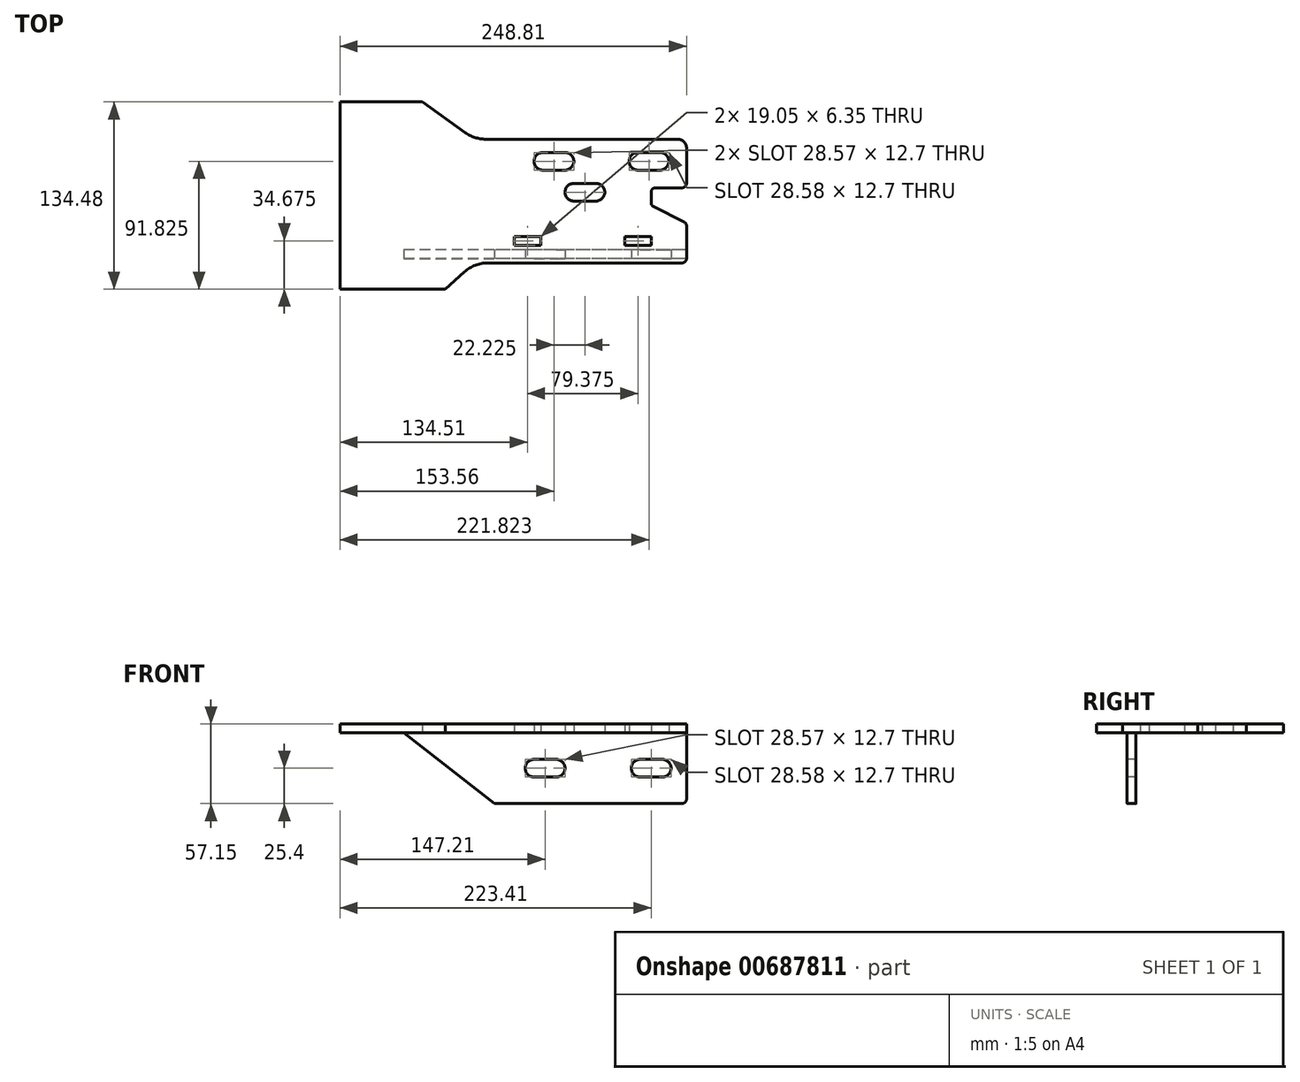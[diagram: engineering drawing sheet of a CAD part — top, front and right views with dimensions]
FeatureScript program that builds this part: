
annotation { "Feature Type Name" : "Feature", "Feature Type Description" : "" }
export const myFeature = defineFeature(function(context is Context, id is Id, definition is map)
    precondition{}
    {
        {
            var Q0;
            Q0=qCreatedBy(makeId("Top.planeOp"),FACE);
            var sketch = newSketch(context, id + "F0", { "sketchPlane" : qUnion([Q0])});
            skLineSegment(sketch, "E0.bottom", {"start": v(-68.04, 44.45) * mm, "end": v(76.2, 44.45) * mm});
            skLineSegment(sketch, "E0.top", {"start": v(-66.48, -44.45) * mm, "end": v(76.2, -44.45) * mm});
            skLineSegment(sketch, "E0.right", {"start": v(76.2, 44.45) * mm, "end": v(76.2, -44.45) * mm});
            skPoint(sketch, "E0.middle", {"position": v(0, 0) * mm});
            skCircle(sketch, "E1", {"center": v(-19.05, 28.58) * mm, "radius": 6.35 * mm});
            skCircle(sketch, "E2", {"center": v(57.15, 28.58) * mm, "radius": 6.35 * mm});
            skCircle(sketch, "E3", {"center": v(3.18, 6.35) * mm, "radius": 6.35 * mm});
            skLineSegment(sketch, "E4.bottom", {"start": v(-28.57, -31.75) * mm, "end": v(-47.62, -31.75) * mm});
            skLineSegment(sketch, "E4.top", {"start": v(-28.57, -25.4) * mm, "end": v(-47.62, -25.4) * mm});
            skLineSegment(sketch, "E4.left", {"start": v(-28.57, -31.75) * mm, "end": v(-28.57, -25.4) * mm});
            skLineSegment(sketch, "E4.right", {"start": v(-47.62, -31.75) * mm, "end": v(-47.62, -25.4) * mm});
            skPoint(sketch, "E4.middle", {"position": v(-38.1, -28.57) * mm});
            skLineSegment(sketch, "E5.bottom", {"start": v(50.8, -31.75) * mm, "end": v(31.75, -31.75) * mm});
            skLineSegment(sketch, "E5.top", {"start": v(50.8, -25.4) * mm, "end": v(31.75, -25.4) * mm});
            skLineSegment(sketch, "E5.left", {"start": v(50.8, -31.75) * mm, "end": v(50.8, -25.4) * mm});
            skLineSegment(sketch, "E5.right", {"start": v(31.75, -31.75) * mm, "end": v(31.75, -25.4) * mm});
            skPoint(sketch, "E5.middle", {"position": v(41.27, -28.57) * mm});
            skLineSegment(sketch, "E6", {"start": v(76.2, 9.53) * mm, "end": v(50.8, 9.53) * mm});
            skLineSegment(sketch, "E7", {"start": v(50.8, 9.52) * mm, "end": v(50.8, -3.18) * mm});
            skLineSegment(sketch, "E8", {"start": v(50.8, -3.18) * mm, "end": v(76.2, -15.88) * mm});
            skLineSegment(sketch, "E9", {"start": v(-82.83, 49.2) * mm, "end": v(-113.59, 71.23) * mm});
            skLineSegment(sketch, "E10", {"start": v(-97.17, -63.25) * mm, "end": v(-83.44, -50.94) * mm});
            skPoint(sketch, "E11.visualSharp", {"position": v(-76.2, 44.45) * mm});
            skArc(sketch, "E11.filletArc", {"start": v(-82.83, 49.2) * mm, "mid": v(-75.8, 45.67) * mm, "end": v(-68.04, 44.45) * mm});
            skPoint(sketch, "E12.visualSharp", {"position": v(-76.2, -44.45) * mm});
            skArc(sketch, "E12.filletArc", {"start": v(-66.48, -44.45) * mm, "mid": v(-75.56, -46.13) * mm, "end": v(-83.44, -50.94) * mm});
            skLineSegment(sketch, "E13", {"start": v(-97.17, -63.25) * mm, "end": v(-172.6, -63.25) * mm});
            skLineSegment(sketch, "E14", {"start": v(-172.6, -63.25) * mm, "end": v(-172.6, 71.23) * mm});
            skLineSegment(sketch, "E15", {"start": v(-172.6, 71.23) * mm, "end": v(-113.59, 71.23) * mm});
            skLineSegment(sketch, "E16", {"start": v(-26.99, 28.57) * mm, "end": v(-11.11, 28.58) * mm});
            skLineSegment(sketch, "E17", {"start": v(41.27, 28.58) * mm, "end": v(57.15, 28.58) * mm});
            skLineSegment(sketch, "E18", {"start": v(-4.76, 6.35) * mm, "end": v(11.11, 6.35) * mm});
            skArc(sketch, "E19.0.startCap", {"start": v(-26.99, 22.23) * mm, "mid": v(-33.34, 28.57) * mm, "end": v(-26.99, 34.93) * mm});
            skArc(sketch, "E19.0.endCap", {"start": v(-11.11, 34.93) * mm, "mid": v(-4.76, 28.57) * mm, "end": v(-11.11, 22.23) * mm});
            skLineSegment(sketch, "E19.0.left", {"start": v(-26.99, 34.92) * mm, "end": v(-11.11, 34.93) * mm});
            skLineSegment(sketch, "E19.0.right", {"start": v(-26.99, 22.23) * mm, "end": v(-11.11, 22.23) * mm});
            skArc(sketch, "E19.1.startCap", {"start": v(-4.76, 0) * mm, "mid": v(-11.11, 6.35) * mm, "end": v(-4.76, 12.7) * mm});
            skArc(sketch, "E19.1.endCap", {"start": v(11.11, 12.7) * mm, "mid": v(17.46, 6.35) * mm, "end": v(11.11, 0) * mm});
            skLineSegment(sketch, "E19.1.left", {"start": v(-4.76, 12.7) * mm, "end": v(11.11, 12.7) * mm});
            skLineSegment(sketch, "E19.1.right", {"start": v(-4.76, 0) * mm, "end": v(11.11, 0) * mm});
            skArc(sketch, "E19.2.startCap", {"start": v(41.27, 22.22) * mm, "mid": v(34.92, 28.57) * mm, "end": v(41.27, 34.92) * mm});
            skArc(sketch, "E19.2.endCap", {"start": v(57.15, 34.93) * mm, "mid": v(63.5, 28.58) * mm, "end": v(57.15, 22.23) * mm});
            skLineSegment(sketch, "E19.2.left", {"start": v(41.27, 34.93) * mm, "end": v(57.15, 34.93) * mm});
            skLineSegment(sketch, "E19.2.right", {"start": v(41.27, 22.23) * mm, "end": v(57.15, 22.23) * mm});
            skSolve(sketch);
        }
        {
            var Q0;
            {var subQ3=sQuery(id+"F0.wireOp",EDGE,"E0.bottom");Q0=makeQuery(id+"F0.imprint","IMPRINT",FACE,{"disambiguationData":[TD([[makeQuery(id+"F0.imprint","IMPRINT",EDGE,{"derivedFrom":subQ3}),-1.0]])]});}
            extrude(context, id + "F1", {"entities" : qUnion([Q0]), "depth" : 6.35 * mm, "offsetDistance" : 25.4 * mm});
        }
        {
            var Q0;
            Q0=makeQuery(id+"F1.opExtrude","CAP_FACE",FACE,{"disambiguationData":[OSD([sQuery(id+"F0.wireOp",EDGE,"E0.bottom"),sQuery(id+"F0.wireOp",EDGE,"E0.top"),sQuery(id+"F0.wireOp",EDGE,"E0.right"),sQuery(id+"F0.wireOp",EDGE,"E2"),sQuery(id+"F0.wireOp",EDGE,"E4.bottom"),sQuery(id+"F0.wireOp",EDGE,"E4.top"),sQuery(id+"F0.wireOp",EDGE,"E4.left"),sQuery(id+"F0.wireOp",EDGE,"E4.right"),sQuery(id+"F0.wireOp",EDGE,"E5.bottom"),sQuery(id+"F0.wireOp",EDGE,"E5.top"),sQuery(id+"F0.wireOp",EDGE,"E5.left"),sQuery(id+"F0.wireOp",EDGE,"E5.right"),sQuery(id+"F0.wireOp",EDGE,"E6"),sQuery(id+"F0.wireOp",EDGE,"E7"),sQuery(id+"F0.wireOp",EDGE,"E8"),sQuery(id+"F0.wireOp",EDGE,"E9"),sQuery(id+"F0.wireOp",EDGE,"E10"),sQuery(id+"F0.wireOp",EDGE,"E11.filletArc"),sQuery(id+"F0.wireOp",EDGE,"E12.filletArc"),sQuery(id+"F0.wireOp",EDGE,"E13"),sQuery(id+"F0.wireOp",EDGE,"E14"),sQuery(id+"F0.wireOp",EDGE,"E15"),sQuery(id+"F0.wireOp",EDGE,"E19.0.startCap"),sQuery(id+"F0.wireOp",EDGE,"E19.0.endCap"),sQuery(id+"F0.wireOp",EDGE,"E19.0.left"),sQuery(id+"F0.wireOp",EDGE,"E19.0.right"),sQuery(id+"F0.wireOp",EDGE,"E19.1.startCap"),sQuery(id+"F0.wireOp",EDGE,"E19.1.endCap"),sQuery(id+"F0.wireOp",EDGE,"E19.1.left"),sQuery(id+"F0.wireOp",EDGE,"E19.1.right"),sQuery(id+"F0.wireOp",EDGE,"E19.2.startCap"),sQuery(id+"F0.wireOp",EDGE,"E19.2.left"),sQuery(id+"F0.wireOp",EDGE,"E19.2.right")])],"isStart":true});
            var sketch = newSketch(context, id + "F2", { "sketchPlane" : qUnion([Q0])});
            skLineSegment(sketch, "E20.bottom", {"start": v(76.2, 41.27) * mm, "end": v(-152, 41.27) * mm});
            skLineSegment(sketch, "E20.top", {"start": v(76.2, 34.92) * mm, "end": v(-152, 34.92) * mm});
            skLineSegment(sketch, "E20.left", {"start": v(76.2, 41.27) * mm, "end": v(76.2, 34.92) * mm});
            skLineSegment(sketch, "E20.right", {"start": v(-152, 41.27) * mm, "end": v(-152, 34.92) * mm});
            skSolve(sketch);
        }
        {
            var Q0;
            Q0 = qSketchRegion(id + "F2", true);
            extrude(context, id + "F3", {"entities" : qUnion([Q0]), "depth" : 50.8 * mm, "offsetDistance" : 25.4 * mm});
        }
        {
            var Q0;
            Q0=makeQuery(id+"F3.opExtrude","SWEPT_FACE",FACE,{"disambiguationData":[OSD([sQuery(id+"F2.wireOp",EDGE,"E20.bottom")])]});
            var sketch = newSketch(context, id + "F4", { "sketchPlane" : qUnion([Q0])});
            skLineSegment(sketch, "E21", {"start": v(58.74, -25.4) * mm, "end": v(50.8, -25.4) * mm});
            skPoint(sketch, "E21.startSnap0", {"position": v(76.2, -25.4) * mm});
            skLineSegment(sketch, "E22", {"start": v(-33.34, -25.4) * mm, "end": v(-25.4, -25.4) * mm});
            skArc(sketch, "E23.0.startCap", {"start": v(-33.34, -31.75) * mm, "mid": v(-39.69, -25.4) * mm, "end": v(-33.34, -19.05) * mm});
            skArc(sketch, "E23.0.endCap", {"start": v(-17.46, -19.05) * mm, "mid": v(-11.11, -25.4) * mm, "end": v(-17.46, -31.75) * mm});
            skLineSegment(sketch, "E23.0.left", {"start": v(-33.34, -19.05) * mm, "end": v(-17.46, -19.05) * mm});
            skLineSegment(sketch, "E23.0.right", {"start": v(-33.34, -31.75) * mm, "end": v(-17.46, -31.75) * mm});
            skArc(sketch, "E23.1.startCap", {"start": v(58.74, -19.05) * mm, "mid": v(65.09, -25.4) * mm, "end": v(58.74, -31.75) * mm});
            skArc(sketch, "E23.1.endCap", {"start": v(42.86, -31.75) * mm, "mid": v(36.51, -25.4) * mm, "end": v(42.86, -19.05) * mm});
            skLineSegment(sketch, "E23.1.left", {"start": v(58.74, -31.75) * mm, "end": v(42.86, -31.75) * mm});
            skLineSegment(sketch, "E23.1.right", {"start": v(58.74, -19.05) * mm, "end": v(42.86, -19.05) * mm});
            skLineSegment(sketch, "E24", {"start": v(-25.4, -25.4) * mm, "end": v(-17.46, -25.4) * mm});
            skLineSegment(sketch, "E25", {"start": v(50.8, -25.4) * mm, "end": v(42.86, -25.4) * mm});
            skLineSegment(sketch, "E26", {"start": v(-126.98, 0) * mm, "end": v(-61.91, -50.8) * mm});
            skSolve(sketch);
        }
        {
            var Q0;
            Q0 = qSketchRegion(id + "F4", true);
            var Q1;
            {var subQ0=sQuery(id+"F4.wireOp",EDGE,"E26");Q1=makeQuery(id+"F4.imprint","IMPRINT",FACE,{"disambiguationData":[TD([[makeQuery(id+"F4.imprint","IMPRINT",EDGE,{"derivedFrom":subQ0}),-1.0]])]});}
            extrude(context, id + "F5", {"entities" : qUnion([Q0, Q1]), "operationType" : NewBodyOperationType.REMOVE, "endBound" : BoundingType.THROUGH_ALL, "oppositeDirection" : true, "depth" : 25.4 * mm, "offsetDistance" : 25.4 * mm});
        }
        {
            var Q0;
            Q0=makeQuery(id+"F1.opExtrude","SWEPT_EDGE",EDGE,{"disambiguationData":[OSD([sQuery(id+"F0.wireOp",EDGE,"E0.bottom"),sQuery(id+"F0.wireOp",EDGE,"E0.right")])]});
            fillet(context, id + "F6", {"entities" : qUnion([Q0]), "radius" : 6.35 * mm, "tangentPropagation" : true, "allowEdgeOverflow" : false});
        }
        {
            var Q0;
            Q0=makeQuery(id+"F1.opExtrude","SWEPT_EDGE",EDGE,{"disambiguationData":[OSD([sQuery(id+"F0.wireOp",EDGE,"E0.right"),sQuery(id+"F0.wireOp",EDGE,"E6")])]});
            var Q1;
            Q1=makeQuery(id+"F1.opExtrude","SWEPT_EDGE",EDGE,{"disambiguationData":[OSD([sQuery(id+"F0.wireOp",EDGE,"E0.right"),sQuery(id+"F0.wireOp",EDGE,"E8")])]});
            var Q2;
            Q2=makeQuery(id+"F1.opExtrude","SWEPT_EDGE",EDGE,{"disambiguationData":[OSD([sQuery(id+"F0.wireOp",EDGE,"E6"),sQuery(id+"F0.wireOp",EDGE,"E7")])]});
            var Q3;
            Q3=makeQuery(id+"F1.opExtrude","SWEPT_EDGE",EDGE,{"disambiguationData":[OSD([sQuery(id+"F0.wireOp",EDGE,"E7"),sQuery(id+"F0.wireOp",EDGE,"E8")])]});
            var Q4;
            Q4=makeQuery(id+"F1.opExtrude","SWEPT_EDGE",EDGE,{"disambiguationData":[OSD([sQuery(id+"F0.wireOp",EDGE,"E0.top"),sQuery(id+"F0.wireOp",EDGE,"E0.right")])]});
            var Q5;
            Q5=makeQuery(id+"F3.opExtrude","CAP_EDGE",EDGE,{"disambiguationData":[OSD([sQuery(id+"F2.wireOp",EDGE,"E20.left")])],"isStart":false});
            var Q6;
            {var subQ0=sQuery(id+"F4.wireOp",EDGE,"E26");var subQ1=sQuery(id+"F2.wireOp",EDGE,"E20.bottom");Q6=makeQuery(id+"F5.boolean.opBoolean","COPY",EDGE,{"derivedFrom":makeQuery(id+"F5.opExtrude","SWEPT_EDGE",EDGE,{"disambiguationData":[OSD([subQ1,subQ0]),TDD([makeQuery(id+"F4.imprint","INTERSECT",VERTEX,{"derivedFrom":[makeQuery(id+"F3.opExtrude","CAP_EDGE",EDGE,{"disambiguationData":[OSD([subQ1])],"isStart":false}),subQ0]})])]})});}
            fillet(context, id + "F7", {"entities" : qUnion([Q0, Q1, Q2, Q3, Q4, Q5, Q6]), "radius" : 3.17 * mm, "tangentPropagation" : true, "allowEdgeOverflow" : false});
        }
    });
